# Revit family: Switch-Isolation_Fan_Scolmore_Click-Polar
name_source: partatom
category: Electrical Fixtures
revit_build: Autodesk Revit 2014 (Build: 20140709_2115(x64)
units: mm (PartAtom-declared; Revit-internal decimal feet)

## types (2) — shared parameters
Apparent Load = 10 VA
Assembly Code = D5010
BackBoxDepth(16-47mm) = 47 mm  [stored 0.154199 ft]
BackBoxHeight = 80 mm  [stored 0.262467 ft]
BackBoxWidth = 80 mm  [stored 0.262467 ft]
Backbox Required = Yes
Default Elevation = 450 mm  [stored 1.47638 ft]
Detail - Fused Spur Visibility = No
Detail - Neon Visibilty = No
Detail - Switch Visibility = Yes
FixtureDepth = 11 mm  [stored 0.0360892 ft]
FixtureHeight = 86 mm  [stored 0.282152 ft]
FixtureMaterial = Phenolic Resin, White
FixtureWidth = 86 mm  [stored 0.282152 ft]
Keynote = 16300
Load Classification = Power
Manufacturer = Scolmore
Number of Poles = 3
Switch Type Label = F
Switch Voltage = 230 V
Type Comments = BS EN 60669
URL = https://www.scolmore.com

## per-type parameters (varying)
| type | Description | Model |
| 10A 3 Pole Fan Isolation Switch | 10A 3 Pole Fan Isolation Switch | Scolmore Click Polar PRW020 |
| 10A 3 Pole Fan Isolation Switch, Unprinted | 10A 3 Pole Fan Isolation Switch, unprinted | Scolmore Click Polar PRW021 |

note: [stored X ft] marks values corroborated as IEEE doubles in the binary element streams (Revit-internal decimal feet)

## geometry (parser evidence)
native form markers: Sweep x4
no freeform markers — native parametric forms only
